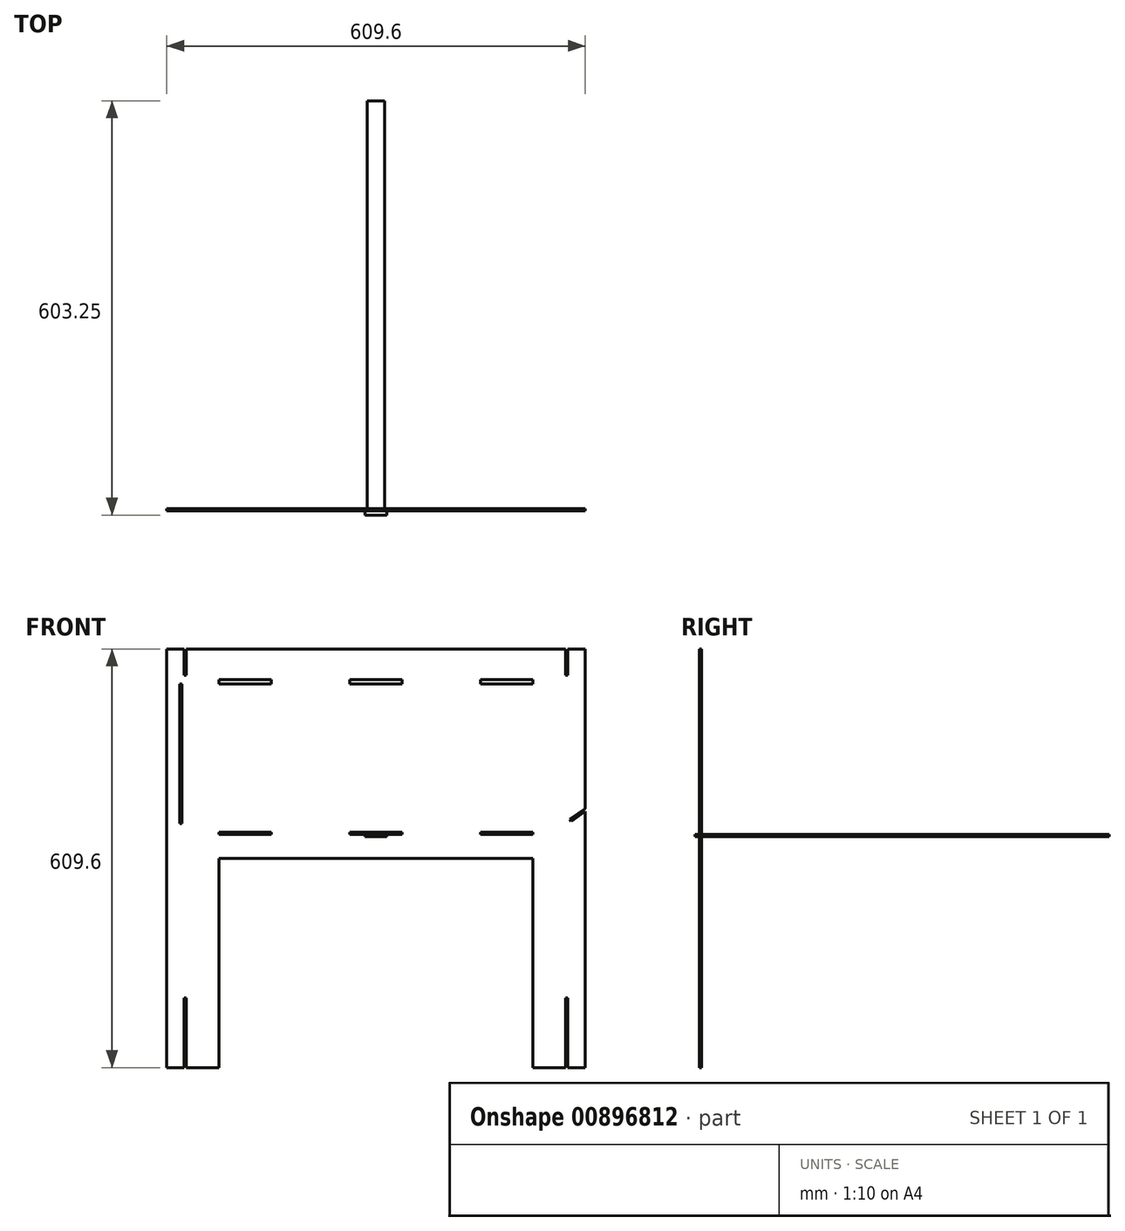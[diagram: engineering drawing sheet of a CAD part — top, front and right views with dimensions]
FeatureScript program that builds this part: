
annotation { "Feature Type Name" : "Feature", "Feature Type Description" : "" }
export const myFeature = defineFeature(function(context is Context, id is Id, definition is map)
    precondition{}
    {
        {
            var Q0;
            Q0=qCreatedBy(makeId("Front.planeOp"),FACE);
            var sketch = newSketch(context, id + "F0", { "sketchPlane" : qUnion([Q0])});
            skLineSegment(sketch, "E0.bottom", {"start": v(304.8, -304.8) * mm, "end": v(-304.8, -304.8) * mm});
            skLineSegment(sketch, "E0.top", {"start": v(304.8, 304.8) * mm, "end": v(-304.8, 304.8) * mm});
            skLineSegment(sketch, "E0.left", {"start": v(304.8, -304.8) * mm, "end": v(304.8, 304.8) * mm});
            skLineSegment(sketch, "E0.right", {"start": v(-304.8, -304.8) * mm, "end": v(-304.8, 304.8) * mm});
            skPoint(sketch, "E0.middle", {"position": v(0, 0) * mm});
            skSolve(sketch);
        }
        {
            var Q0;
            Q0=makeQuery(id+"F0.imprint","IMPRINT",FACE,{"disambiguationData":[TD([[makeQuery(id+"F0.imprint","IMPRINT",EDGE,{"derivedFrom":sQuery(id+"F0.wireOp",EDGE,"E0.bottom")}),-1.0]])]});
            extrude(context, id + "F1", {"entities" : qUnion([Q0]), "depth" : 3.17 * mm, "offsetDistance" : 25.4 * mm});
        }
        {
            var Q0;
            Q0=makeQuery(id+"F1.opExtrude","CAP_FACE",FACE,{"disambiguationData":[OSD([sQuery(id+"F0.wireOp",EDGE,"E0.bottom"),sQuery(id+"F0.wireOp",EDGE,"E0.top"),sQuery(id+"F0.wireOp",EDGE,"E0.left"),sQuery(id+"F0.wireOp",EDGE,"E0.right")])],"isStart":false});
            var sketch = newSketch(context, id + "F2", { "sketchPlane" : qUnion([Q0])});
            skLineSegment(sketch, "E1.bottom", {"start": v(-228.6, -304.8) * mm, "end": v(228.6, -304.8) * mm});
            skLineSegment(sketch, "E1.top", {"start": v(-228.6, 0) * mm, "end": v(228.6, 0) * mm});
            skLineSegment(sketch, "E1.left", {"start": v(-228.6, -304.8) * mm, "end": v(-228.6, 0) * mm});
            skLineSegment(sketch, "E1.right", {"start": v(228.6, -304.8) * mm, "end": v(228.6, 0) * mm});
            skLineSegment(sketch, "E2.bottom", {"start": v(-279.4, 304.8) * mm, "end": v(-276.23, 304.8) * mm});
            skLineSegment(sketch, "E2.top", {"start": v(-279.4, 152.4) * mm, "end": v(-276.23, 152.4) * mm});
            skLineSegment(sketch, "E2.left", {"start": v(-279.4, 304.8) * mm, "end": v(-279.4, 152.4) * mm});
            skLineSegment(sketch, "E2.right", {"start": v(-276.23, 304.8) * mm, "end": v(-276.23, 152.4) * mm});
            skLineSegment(sketch, "E3.bottom", {"start": v(276.23, 304.8) * mm, "end": v(279.4, 304.8) * mm});
            skLineSegment(sketch, "E3.top", {"start": v(276.23, 152.4) * mm, "end": v(279.4, 152.4) * mm});
            skLineSegment(sketch, "E3.left", {"start": v(276.23, 304.8) * mm, "end": v(276.23, 152.4) * mm});
            skLineSegment(sketch, "E3.right", {"start": v(279.4, 304.8) * mm, "end": v(279.4, 152.4) * mm});
            skLineSegment(sketch, "E4", {"start": v(304.8, 116.58) * mm, "end": v(304.8, 127) * mm});
            skLineSegment(sketch, "E5.0.0", {"start": v(304.8, -304.8) * mm, "end": v(304.8, 304.8) * mm, "construction": true});
            skLineSegment(sketch, "E5.0.1", {"start": v(304.8, 304.8) * mm, "end": v(-304.8, 304.8) * mm, "construction": true});
            skLineSegment(sketch, "E5.0.2", {"start": v(-304.8, 304.8) * mm, "end": v(-304.8, -304.8) * mm, "construction": true});
            skLineSegment(sketch, "E5.0.3", {"start": v(-304.8, -304.8) * mm, "end": v(304.8, -304.8) * mm, "construction": true});
            skLineSegment(sketch, "E6", {"start": v(304.8, 122.5) * mm, "end": v(304.8, 127) * mm});
            skLineSegment(sketch, "E7", {"start": v(304.8, 50.8) * mm, "end": v(279.4, 50.8) * mm, "construction": true});
            skLineSegment(sketch, "E8", {"start": v(284, 54.02) * mm, "end": v(304.8, 68.59) * mm, "construction": true});
            skLineSegment(sketch, "E9", {"start": v(304.8, 68.59) * mm, "end": v(284, 54.02) * mm});
            skLineSegment(sketch, "E10", {"start": v(284, 54.02) * mm, "end": v(282.17, 56.62) * mm});
            skLineSegment(sketch, "E11", {"start": v(282.17, 56.62) * mm, "end": v(304.8, 72.46) * mm});
            skLineSegment(sketch, "E12", {"start": v(304.8, 72.46) * mm, "end": v(304.8, 68.59) * mm});
            skLineSegment(sketch, "E13", {"start": v(0, 0) * mm, "end": v(0, 38.1) * mm, "construction": true});
            skLineSegment(sketch, "E14", {"start": v(-228.6, 0) * mm, "end": v(-228.6, 38.1) * mm, "construction": true});
            skLineSegment(sketch, "E15.bottom", {"start": v(-228.6, 38.1) * mm, "end": v(-152.4, 38.1) * mm});
            skLineSegment(sketch, "E15.top", {"start": v(-228.6, 34.92) * mm, "end": v(-152.4, 34.92) * mm});
            skLineSegment(sketch, "E15.left", {"start": v(-228.6, 38.1) * mm, "end": v(-228.6, 34.92) * mm});
            skLineSegment(sketch, "E15.right", {"start": v(-152.4, 38.1) * mm, "end": v(-152.4, 34.92) * mm});
            skLineSegment(sketch, "E16.bottom", {"start": v(38.1, 38.1) * mm, "end": v(-38.1, 38.1) * mm});
            skLineSegment(sketch, "E16.top", {"start": v(38.1, 34.92) * mm, "end": v(-38.1, 34.92) * mm});
            skLineSegment(sketch, "E16.left", {"start": v(38.1, 38.1) * mm, "end": v(38.1, 34.92) * mm});
            skLineSegment(sketch, "E16.right", {"start": v(-38.1, 38.1) * mm, "end": v(-38.1, 34.92) * mm});
            skPoint(sketch, "E16.middle", {"position": v(0, 36.51) * mm});
            skLineSegment(sketch, "E17.bottom", {"start": v(228.6, 38.1) * mm, "end": v(152.4, 38.1) * mm});
            skLineSegment(sketch, "E17.top", {"start": v(228.6, 34.92) * mm, "end": v(152.4, 34.92) * mm});
            skLineSegment(sketch, "E17.left", {"start": v(228.6, 38.1) * mm, "end": v(228.6, 34.92) * mm});
            skLineSegment(sketch, "E17.right", {"start": v(152.4, 38.1) * mm, "end": v(152.4, 34.92) * mm});
            skLineSegment(sketch, "E18", {"start": v(0, 304.8) * mm, "end": v(0, 254) * mm, "construction": true});
            skLineSegment(sketch, "E19.bottom", {"start": v(-38.1, 260.38) * mm, "end": v(38.1, 260.32) * mm});
            skLineSegment(sketch, "E19.left", {"start": v(-38.1, 260.38) * mm, "end": v(-38.1, 254.03) * mm});
            skLineSegment(sketch, "E19.right", {"start": v(38.1, 260.32) * mm, "end": v(38.1, 253.97) * mm});
            skPoint(sketch, "E19.middle", {"position": v(0, 254) * mm});
            skLineSegment(sketch, "E20", {"start": v(-38.1, 254.03) * mm, "end": v(38.1, 253.97) * mm});
            skPoint(sketch, "E19.top.end.orphan", {"position": v(38.1, 247.62) * mm});
            skPoint(sketch, "E21.orphan", {"position": v(-38.1, 247.68) * mm});
            skLineSegment(sketch, "E22.bottom", {"start": v(-228.6, 254.03) * mm, "end": v(-152.4, 254.03) * mm});
            skLineSegment(sketch, "E22.top", {"start": v(-228.6, 260.38) * mm, "end": v(-152.4, 260.38) * mm});
            skLineSegment(sketch, "E22.left", {"start": v(-228.6, 254.03) * mm, "end": v(-228.6, 260.38) * mm});
            skLineSegment(sketch, "E22.right", {"start": v(-152.4, 254.03) * mm, "end": v(-152.4, 260.38) * mm});
            skLineSegment(sketch, "E23.bottom", {"start": v(152.4, 253.97) * mm, "end": v(228.6, 253.97) * mm});
            skLineSegment(sketch, "E23.top", {"start": v(152.4, 260.32) * mm, "end": v(228.6, 260.32) * mm});
            skLineSegment(sketch, "E23.left", {"start": v(152.4, 253.97) * mm, "end": v(152.4, 260.32) * mm});
            skLineSegment(sketch, "E23.right", {"start": v(228.6, 253.97) * mm, "end": v(228.6, 260.32) * mm});
            skSolve(sketch);
        }
        {
            var Q0;
            Q0 = qSketchRegion(id + "F2", true);
            extrude(context, id + "F3", {"entities" : qUnion([Q0]), "operationType" : NewBodyOperationType.REMOVE, "endBound" : BoundingType.THROUGH_ALL, "oppositeDirection" : true, "depth" : 25.4 * mm, "offsetDistance" : 25.4 * mm});
        }
        {
            var Q0;
            Q0=makeQuery(id+"F1.opExtrude","CAP_FACE",FACE,{"disambiguationData":[OSD([sQuery(id+"F0.wireOp",EDGE,"E0.bottom"),sQuery(id+"F0.wireOp",EDGE,"E0.top"),sQuery(id+"F0.wireOp",EDGE,"E0.left"),sQuery(id+"F0.wireOp",EDGE,"E0.right")])],"isStart":false});
            var sketch = newSketch(context, id + "F4", { "sketchPlane" : qUnion([Q0])});
            skLineSegment(sketch, "E24.bottom", {"start": v(-279.4, -304.8) * mm, "end": v(-276.23, -304.8) * mm});
            skLineSegment(sketch, "E24.top", {"start": v(-279.4, -203.2) * mm, "end": v(-276.23, -203.2) * mm});
            skLineSegment(sketch, "E24.left", {"start": v(-279.4, -304.8) * mm, "end": v(-279.4, -203.2) * mm});
            skLineSegment(sketch, "E24.right", {"start": v(-276.23, -304.8) * mm, "end": v(-276.23, -203.2) * mm});
            skLineSegment(sketch, "E25.0.0", {"start": v(228.6, 0) * mm, "end": v(228.6, -304.8) * mm, "construction": true});
            skLineSegment(sketch, "E25.0.1", {"start": v(228.6, -304.8) * mm, "end": v(304.8, -304.8) * mm, "construction": true});
            skLineSegment(sketch, "E25.0.2", {"start": v(304.8, -304.8) * mm, "end": v(304.8, 68.59) * mm, "construction": true});
            skLineSegment(sketch, "E25.0.3", {"start": v(304.8, 68.59) * mm, "end": v(284, 54.02) * mm, "construction": true});
            skLineSegment(sketch, "E25.0.4", {"start": v(284, 54.02) * mm, "end": v(282.17, 56.62) * mm, "construction": true});
            skLineSegment(sketch, "E25.0.5", {"start": v(282.17, 56.62) * mm, "end": v(304.8, 72.46) * mm, "construction": true});
            skLineSegment(sketch, "E25.0.6", {"start": v(304.8, 72.46) * mm, "end": v(304.8, 304.8) * mm, "construction": true});
            skLineSegment(sketch, "E25.0.7", {"start": v(304.8, 304.8) * mm, "end": v(279.4, 304.8) * mm, "construction": true});
            skLineSegment(sketch, "E25.0.8", {"start": v(279.4, 304.8) * mm, "end": v(279.4, 152.4) * mm, "construction": true});
            skLineSegment(sketch, "E25.0.9", {"start": v(279.4, 152.4) * mm, "end": v(276.23, 152.4) * mm, "construction": true});
            skLineSegment(sketch, "E25.0.10", {"start": v(276.23, 152.4) * mm, "end": v(276.23, 304.8) * mm, "construction": true});
            skLineSegment(sketch, "E25.0.11", {"start": v(276.23, 304.8) * mm, "end": v(-276.23, 304.8) * mm, "construction": true});
            skLineSegment(sketch, "E25.0.12", {"start": v(-276.23, 304.8) * mm, "end": v(-276.23, 152.4) * mm, "construction": true});
            skLineSegment(sketch, "E25.0.13", {"start": v(-276.23, 152.4) * mm, "end": v(-279.4, 152.4) * mm, "construction": true});
            skLineSegment(sketch, "E25.0.14", {"start": v(-279.4, 152.4) * mm, "end": v(-279.4, 304.8) * mm, "construction": true});
            skLineSegment(sketch, "E25.0.15", {"start": v(-279.4, 304.8) * mm, "end": v(-304.8, 304.8) * mm, "construction": true});
            skLineSegment(sketch, "E25.0.16", {"start": v(-304.8, 304.8) * mm, "end": v(-304.8, -304.8) * mm, "construction": true});
            skLineSegment(sketch, "E25.0.17", {"start": v(-304.8, -304.8) * mm, "end": v(-228.6, -304.8) * mm, "construction": true});
            skLineSegment(sketch, "E25.0.18", {"start": v(-228.6, -304.8) * mm, "end": v(-228.6, 0) * mm, "construction": true});
            skLineSegment(sketch, "E25.0.19", {"start": v(-228.6, 0) * mm, "end": v(228.6, 0) * mm, "construction": true});
            skLineSegment(sketch, "E26.bottom", {"start": v(276.23, -304.8) * mm, "end": v(279.4, -304.8) * mm});
            skLineSegment(sketch, "E26.top", {"start": v(276.23, -203.2) * mm, "end": v(279.4, -203.2) * mm});
            skLineSegment(sketch, "E26.left", {"start": v(276.23, -304.8) * mm, "end": v(276.23, -203.2) * mm});
            skLineSegment(sketch, "E26.right", {"start": v(279.4, -304.8) * mm, "end": v(279.4, -203.2) * mm});
            skSolve(sketch);
        }
        {
            var Q0;
            Q0 = qSketchRegion(id + "F4", true);
            extrude(context, id + "F5", {"entities" : qUnion([Q0]), "operationType" : NewBodyOperationType.REMOVE, "endBound" : BoundingType.THROUGH_ALL, "oppositeDirection" : true, "depth" : 25.4 * mm, "offsetDistance" : 25.4 * mm});
        }
        {
            var Q0;
            Q0=makeQuery(id+"F1.opExtrude","CAP_FACE",FACE,{"disambiguationData":[OSD([sQuery(id+"F0.wireOp",EDGE,"E0.bottom"),sQuery(id+"F0.wireOp",EDGE,"E0.top"),sQuery(id+"F0.wireOp",EDGE,"E0.left"),sQuery(id+"F0.wireOp",EDGE,"E0.right")])],"isStart":false});
            var sketch = newSketch(context, id + "F6", { "sketchPlane" : qUnion([Q0])});
            skLineSegment(sketch, "E27.0.0", {"start": v(-276.23, -203.2) * mm, "end": v(-276.23, -304.8) * mm, "construction": true});
            skLineSegment(sketch, "E27.0.1", {"start": v(-276.23, -304.8) * mm, "end": v(-228.6, -304.8) * mm, "construction": true});
            skLineSegment(sketch, "E27.0.2", {"start": v(-228.6, -304.8) * mm, "end": v(-228.6, 0) * mm, "construction": true});
            skLineSegment(sketch, "E27.0.3", {"start": v(-228.6, 0) * mm, "end": v(228.6, 0) * mm, "construction": true});
            skLineSegment(sketch, "E27.0.4", {"start": v(228.6, 0) * mm, "end": v(228.6, -304.8) * mm, "construction": true});
            skLineSegment(sketch, "E27.0.5", {"start": v(228.6, -304.8) * mm, "end": v(276.23, -304.8) * mm, "construction": true});
            skLineSegment(sketch, "E27.0.6", {"start": v(276.23, -304.8) * mm, "end": v(276.23, -203.2) * mm, "construction": true});
            skLineSegment(sketch, "E27.0.7", {"start": v(276.23, -203.2) * mm, "end": v(279.4, -203.2) * mm, "construction": true});
            skLineSegment(sketch, "E27.0.8", {"start": v(279.4, -203.2) * mm, "end": v(279.4, -304.8) * mm, "construction": true});
            skLineSegment(sketch, "E27.0.9", {"start": v(279.4, -304.8) * mm, "end": v(304.8, -304.8) * mm, "construction": true});
            skLineSegment(sketch, "E27.0.10", {"start": v(304.8, -304.8) * mm, "end": v(304.8, 68.59) * mm, "construction": true});
            skLineSegment(sketch, "E27.0.11", {"start": v(304.8, 68.59) * mm, "end": v(284, 54.02) * mm, "construction": true});
            skLineSegment(sketch, "E27.0.12", {"start": v(284, 54.02) * mm, "end": v(282.17, 56.62) * mm, "construction": true});
            skLineSegment(sketch, "E27.0.13", {"start": v(282.17, 56.62) * mm, "end": v(304.8, 72.46) * mm, "construction": true});
            skLineSegment(sketch, "E27.0.14", {"start": v(304.8, 72.46) * mm, "end": v(304.8, 304.8) * mm, "construction": true});
            skLineSegment(sketch, "E27.0.15", {"start": v(304.8, 304.8) * mm, "end": v(279.4, 304.8) * mm, "construction": true});
            skLineSegment(sketch, "E27.0.16", {"start": v(279.4, 304.8) * mm, "end": v(279.4, 152.4) * mm, "construction": true});
            skLineSegment(sketch, "E27.0.17", {"start": v(279.4, 152.4) * mm, "end": v(276.23, 152.4) * mm, "construction": true});
            skLineSegment(sketch, "E27.0.18", {"start": v(276.23, 152.4) * mm, "end": v(276.23, 304.8) * mm, "construction": true});
            skLineSegment(sketch, "E27.0.19", {"start": v(276.23, 304.8) * mm, "end": v(-276.23, 304.8) * mm, "construction": true});
            skLineSegment(sketch, "E27.0.20", {"start": v(-276.23, 304.8) * mm, "end": v(-276.23, 152.4) * mm, "construction": true});
            skLineSegment(sketch, "E27.0.21", {"start": v(-276.23, 152.4) * mm, "end": v(-279.4, 152.4) * mm, "construction": true});
            skLineSegment(sketch, "E27.0.22", {"start": v(-279.4, 152.4) * mm, "end": v(-279.4, 304.8) * mm, "construction": true});
            skLineSegment(sketch, "E27.0.23", {"start": v(-279.4, 304.8) * mm, "end": v(-304.8, 304.8) * mm, "construction": true});
            skLineSegment(sketch, "E27.0.24", {"start": v(-304.8, 304.8) * mm, "end": v(-304.8, -304.8) * mm, "construction": true});
            skLineSegment(sketch, "E27.0.25", {"start": v(-304.8, -304.8) * mm, "end": v(-279.4, -304.8) * mm, "construction": true});
            skLineSegment(sketch, "E27.0.26", {"start": v(-279.4, -304.8) * mm, "end": v(-279.4, -203.2) * mm, "construction": true});
            skLineSegment(sketch, "E27.0.27", {"start": v(-279.4, -203.2) * mm, "end": v(-276.23, -203.2) * mm, "construction": true});
            skLineSegment(sketch, "E28.bottom", {"start": v(-282.58, 254) * mm, "end": v(-285.75, 254) * mm});
            skLineSegment(sketch, "E28.top", {"start": v(-282.58, 50.8) * mm, "end": v(-285.75, 50.8) * mm});
            skLineSegment(sketch, "E28.left", {"start": v(-282.58, 254) * mm, "end": v(-282.58, 50.8) * mm});
            skLineSegment(sketch, "E28.right", {"start": v(-285.75, 254) * mm, "end": v(-285.75, 50.8) * mm});
            skSolve(sketch);
        }
        {
            var Q0;
            Q0 = qSketchRegion(id + "F6", true);
            extrude(context, id + "F7", {"entities" : qUnion([Q0]), "operationType" : NewBodyOperationType.REMOVE, "endBound" : BoundingType.THROUGH_ALL, "oppositeDirection" : true, "depth" : 25.4 * mm, "offsetDistance" : 25.4 * mm});
        }
        {
            var Q0;
            Q0=makeQuery(id+"F1.opExtrude","CAP_FACE",FACE,{"disambiguationData":[OSD([sQuery(id+"F0.wireOp",EDGE,"E0.bottom"),sQuery(id+"F0.wireOp",EDGE,"E0.top"),sQuery(id+"F0.wireOp",EDGE,"E0.left"),sQuery(id+"F0.wireOp",EDGE,"E0.right")])],"isStart":false});
            var sketch = newSketch(context, id + "F8", { "sketchPlane" : qUnion([Q0])});
            skLineSegment(sketch, "E29.0.0", {"start": v(-276.23, -203.2) * mm, "end": v(-276.23, -304.8) * mm, "construction": true});
            skLineSegment(sketch, "E29.0.1", {"start": v(-276.23, -304.8) * mm, "end": v(-228.6, -304.8) * mm, "construction": true});
            skLineSegment(sketch, "E29.0.2", {"start": v(-228.6, -304.8) * mm, "end": v(-228.6, 0) * mm, "construction": true});
            skLineSegment(sketch, "E29.0.3", {"start": v(-228.6, 0) * mm, "end": v(228.6, 0) * mm, "construction": true});
            skLineSegment(sketch, "E29.0.4", {"start": v(228.6, 0) * mm, "end": v(228.6, -304.8) * mm, "construction": true});
            skLineSegment(sketch, "E29.0.5", {"start": v(228.6, -304.8) * mm, "end": v(276.23, -304.8) * mm, "construction": true});
            skLineSegment(sketch, "E29.0.6", {"start": v(276.23, -304.8) * mm, "end": v(276.23, -203.2) * mm, "construction": true});
            skLineSegment(sketch, "E29.0.7", {"start": v(276.23, -203.2) * mm, "end": v(279.4, -203.2) * mm, "construction": true});
            skLineSegment(sketch, "E29.0.8", {"start": v(279.4, -203.2) * mm, "end": v(279.4, -304.8) * mm, "construction": true});
            skLineSegment(sketch, "E29.0.9", {"start": v(279.4, -304.8) * mm, "end": v(304.8, -304.8) * mm, "construction": true});
            skLineSegment(sketch, "E29.0.10", {"start": v(304.8, -304.8) * mm, "end": v(304.8, 68.59) * mm, "construction": true});
            skLineSegment(sketch, "E29.0.11", {"start": v(304.8, 68.59) * mm, "end": v(284, 54.02) * mm, "construction": true});
            skLineSegment(sketch, "E29.0.12", {"start": v(284, 54.02) * mm, "end": v(282.17, 56.62) * mm, "construction": true});
            skLineSegment(sketch, "E29.0.13", {"start": v(282.17, 56.62) * mm, "end": v(304.8, 72.46) * mm, "construction": true});
            skLineSegment(sketch, "E29.0.14", {"start": v(304.8, 72.46) * mm, "end": v(304.8, 304.8) * mm, "construction": true});
            skLineSegment(sketch, "E29.0.15", {"start": v(304.8, 304.8) * mm, "end": v(279.4, 304.8) * mm, "construction": true});
            skLineSegment(sketch, "E29.0.16", {"start": v(279.4, 304.8) * mm, "end": v(279.4, 152.4) * mm, "construction": true});
            skLineSegment(sketch, "E29.0.17", {"start": v(279.4, 152.4) * mm, "end": v(276.23, 152.4) * mm, "construction": true});
            skLineSegment(sketch, "E29.0.18", {"start": v(276.23, 152.4) * mm, "end": v(276.23, 304.8) * mm, "construction": true});
            skLineSegment(sketch, "E29.0.19", {"start": v(276.23, 304.8) * mm, "end": v(-276.23, 304.8) * mm, "construction": true});
            skLineSegment(sketch, "E29.0.20", {"start": v(-276.23, 304.8) * mm, "end": v(-276.23, 152.4) * mm, "construction": true});
            skLineSegment(sketch, "E29.0.21", {"start": v(-276.23, 152.4) * mm, "end": v(-279.4, 152.4) * mm, "construction": true});
            skLineSegment(sketch, "E29.0.22", {"start": v(-279.4, 152.4) * mm, "end": v(-279.4, 304.8) * mm, "construction": true});
            skLineSegment(sketch, "E29.0.23", {"start": v(-279.4, 304.8) * mm, "end": v(-304.8, 304.8) * mm, "construction": true});
            skLineSegment(sketch, "E29.0.24", {"start": v(-304.8, 304.8) * mm, "end": v(-304.8, -304.8) * mm, "construction": true});
            skLineSegment(sketch, "E29.0.25", {"start": v(-304.8, -304.8) * mm, "end": v(-279.4, -304.8) * mm, "construction": true});
            skLineSegment(sketch, "E29.0.26", {"start": v(-279.4, -304.8) * mm, "end": v(-279.4, -203.2) * mm, "construction": true});
            skLineSegment(sketch, "E29.0.27", {"start": v(-279.4, -203.2) * mm, "end": v(-276.23, -203.2) * mm, "construction": true});
            skLineSegment(sketch, "E30.0", {"start": v(-228.6, 38.1) * mm, "end": v(-152.4, 38.1) * mm, "construction": true});
            skLineSegment(sketch, "E31.0", {"start": v(-228.6, 34.92) * mm, "end": v(-152.4, 34.92) * mm, "construction": true});
            skPoint(sketch, "E32.0", {"position": v(-152.4, 36.51) * mm});
            skLineSegment(sketch, "E33.0", {"start": v(-152.4, 38.1) * mm, "end": v(-152.4, 34.92) * mm, "construction": true});
            skLineSegment(sketch, "E34.0", {"start": v(-228.6, 38.1) * mm, "end": v(-228.6, 34.92) * mm, "construction": true});
            skLineSegment(sketch, "E35.0", {"start": v(38.1, 38.1) * mm, "end": v(-38.1, 38.1) * mm, "construction": true});
            skLineSegment(sketch, "E36.0", {"start": v(38.1, 38.1) * mm, "end": v(38.1, 34.92) * mm, "construction": true});
            skLineSegment(sketch, "E37.0", {"start": v(38.1, 34.92) * mm, "end": v(-38.1, 34.92) * mm, "construction": true});
            skLineSegment(sketch, "E38.0", {"start": v(-38.1, 38.1) * mm, "end": v(-38.1, 34.92) * mm, "construction": true});
            skLineSegment(sketch, "E39.0", {"start": v(152.4, 38.1) * mm, "end": v(152.4, 34.92) * mm, "construction": true});
            skLineSegment(sketch, "E40.0", {"start": v(228.6, 34.92) * mm, "end": v(152.4, 34.92) * mm, "construction": true});
            skLineSegment(sketch, "E41.0", {"start": v(228.6, 38.1) * mm, "end": v(152.4, 38.1) * mm, "construction": true});
            skLineSegment(sketch, "E42.0", {"start": v(228.6, 38.1) * mm, "end": v(228.6, 34.92) * mm, "construction": true});
            skLineSegment(sketch, "E43.bottom", {"start": v(-12.7, 34.92) * mm, "end": v(12.7, 34.92) * mm});
            skLineSegment(sketch, "E43.top", {"start": v(-12.7, 31.75) * mm, "end": v(12.7, 31.75) * mm});
            skLineSegment(sketch, "E43.left", {"start": v(-12.7, 34.92) * mm, "end": v(-12.7, 31.75) * mm});
            skLineSegment(sketch, "E43.right", {"start": v(12.7, 34.92) * mm, "end": v(12.7, 31.75) * mm});
            skSolve(sketch);
        }
        {
            var Q0;
            Q0 = qSketchRegion(id + "F8", true);
            extrude(context, id + "F9", {"entities" : qUnion([Q0]), "operationType" : NewBodyOperationType.REMOVE, "endBound" : BoundingType.THROUGH_ALL, "oppositeDirection" : true, "depth" : 25.4 * mm, "offsetDistance" : 25.4 * mm});
        }
        {
            var Q0;
            Q0 = qSketchRegion(id + "F8", true);
            extrude(context, id + "F10", {"entities" : qUnion([Q0]), "oppositeDirection" : true, "depth" : 596.9 * mm, "offsetDistance" : 25.4 * mm});
        }
        {
            var Q0;
            Q0=makeQuery(id+"F10.opExtrude","CAP_FACE",FACE,{"disambiguationData":[OSD([sQuery(id+"F8.wireOp",EDGE,"E43.bottom"),sQuery(id+"F8.wireOp",EDGE,"E43.top"),sQuery(id+"F8.wireOp",EDGE,"E43.left"),sQuery(id+"F8.wireOp",EDGE,"E43.right")])],"isStart":true});
            var sketch = newSketch(context, id + "F11", { "sketchPlane" : qUnion([Q0])});
            skLineSegment(sketch, "E44.0.0", {"start": v(12.7, 31.75) * mm, "end": v(12.7, 34.92) * mm, "construction": true});
            skLineSegment(sketch, "E44.0.1", {"start": v(12.7, 34.92) * mm, "end": v(-12.7, 34.92) * mm, "construction": true});
            skLineSegment(sketch, "E44.0.2", {"start": v(-12.7, 34.92) * mm, "end": v(-12.7, 31.75) * mm, "construction": true});
            skLineSegment(sketch, "E44.0.3", {"start": v(-12.7, 31.75) * mm, "end": v(12.7, 31.75) * mm, "construction": true});
            skLineSegment(sketch, "E45.0", {"start": v(-12.7, 34.92) * mm, "end": v(-38.1, 34.92) * mm, "construction": true});
            skLineSegment(sketch, "E46.0", {"start": v(38.1, 34.92) * mm, "end": v(12.7, 34.92) * mm, "construction": true});
            skLineSegment(sketch, "E47.bottom", {"start": v(-15.88, 34.92) * mm, "end": v(15.88, 34.92) * mm});
            skLineSegment(sketch, "E47.top", {"start": v(-15.88, 31.75) * mm, "end": v(15.88, 31.75) * mm});
            skLineSegment(sketch, "E47.left", {"start": v(-15.88, 34.92) * mm, "end": v(-15.88, 31.75) * mm});
            skLineSegment(sketch, "E47.right", {"start": v(15.88, 34.92) * mm, "end": v(15.88, 31.75) * mm});
            skSolve(sketch);
        }
        {
            var Q0;
            Q0 = qSketchRegion(id + "F11", true);
            extrude(context, id + "F12", {"entities" : qUnion([Q0]), "operationType" : NewBodyOperationType.ADD, "depth" : 6.35 * mm, "offsetDistance" : 25.4 * mm});
        }
        {
            var Q0;
            Q0=makeQuery(id+"F1.opExtrude","CAP_FACE",FACE,{"disambiguationData":[OSD([sQuery(id+"F0.wireOp",EDGE,"E0.bottom"),sQuery(id+"F0.wireOp",EDGE,"E0.top"),sQuery(id+"F0.wireOp",EDGE,"E0.left"),sQuery(id+"F0.wireOp",EDGE,"E0.right")])],"isStart":false});
            var sketch = newSketch(context, id + "F13", { "sketchPlane" : qUnion([Q0])});
            skLineSegment(sketch, "E48.0", {"start": v(-276.23, 304.8) * mm, "end": v(-276.23, 152.4) * mm, "construction": true});
            skLineSegment(sketch, "E49.0", {"start": v(-279.4, 304.8) * mm, "end": v(-279.4, 152.4) * mm, "construction": true});
            skLineSegment(sketch, "E50.0", {"start": v(-279.4, 152.4) * mm, "end": v(-276.23, 152.4) * mm, "construction": true});
            skLineSegment(sketch, "E51.0", {"start": v(276.23, 304.8) * mm, "end": v(276.23, 152.4) * mm, "construction": true});
            skLineSegment(sketch, "E52.0", {"start": v(276.23, 152.4) * mm, "end": v(279.4, 152.4) * mm, "construction": true});
            skLineSegment(sketch, "E53.0", {"start": v(279.4, 304.8) * mm, "end": v(279.4, 152.4) * mm, "construction": true});
            skLineSegment(sketch, "E54.bottom", {"start": v(-279.4, 152.4) * mm, "end": v(-276.23, 152.4) * mm});
            skLineSegment(sketch, "E54.top", {"start": v(-279.4, 266.7) * mm, "end": v(-276.23, 266.7) * mm});
            skLineSegment(sketch, "E54.left", {"start": v(-279.4, 152.4) * mm, "end": v(-279.4, 266.7) * mm});
            skLineSegment(sketch, "E54.right", {"start": v(-276.23, 152.4) * mm, "end": v(-276.23, 266.7) * mm});
            skLineSegment(sketch, "E55.bottom", {"start": v(276.23, 152.4) * mm, "end": v(279.4, 152.4) * mm});
            skLineSegment(sketch, "E55.top", {"start": v(276.23, 266.7) * mm, "end": v(279.4, 266.7) * mm});
            skLineSegment(sketch, "E55.left", {"start": v(276.23, 152.4) * mm, "end": v(276.23, 266.7) * mm});
            skLineSegment(sketch, "E55.right", {"start": v(279.4, 152.4) * mm, "end": v(279.4, 266.7) * mm});
            skSolve(sketch);
        }
        {
            var Q0;
            Q0 = qSketchRegion(id + "F13", true);
            extrude(context, id + "F14", {"entities" : qUnion([Q0]), "operationType" : NewBodyOperationType.ADD, "oppositeDirection" : true, "depth" : 3.17 * mm, "offsetDistance" : 25.4 * mm});
        }
    });
